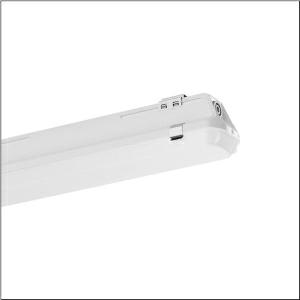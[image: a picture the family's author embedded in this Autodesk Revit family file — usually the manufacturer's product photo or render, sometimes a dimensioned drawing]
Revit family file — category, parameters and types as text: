
# Revit family: monsun_r__21_51fb10dp480b_f32f
name_source: partatom
category: Lighting Fixtures
units: mm (PartAtom-declared; Revit-internal decimal feet)

## family parameters
Cut with Voids When Loaded = No
Host = Face
Light Source = No
Part Type = Normal
Room Calculation Point = No
Round Connector Dimension = Use Diameter
Shared = No

## types (1)
- --- (1 x LED, 8090 lm, 54.4 W, 4000K)
    Apparent Load = 54 VA
    CIE Flux Codes = 47 77 93 94 100
    Color Rendering = 80
    Color Temperature = 4000K
    Default Elevation = 1800 mm
    Description = Monsun® 21, damp-proof luminaire, chain hanger, primary optical cover: enclosure, of PMMA, light emission: direct distribution, primary light characteristic: symmetric, installation type: suspended mounting, surface-mounted, horizontal mounting, vertical mounting, LED, rated luminous flux: 8.090lm, luminous efficacy: 149lm/W, light colour: 840, colour temperature: 4000K, control gear: ECG DALI, with terminal, 5-pole, max. 2.5mm², mains connection: 220..240V, AC, 50/60Hz, rated input power: 54W, housing, of glass-fibre reinforced polyester, uncoated, bright grey, incl. chain hanger, length: 1.590mm, width: 90mm, height: 88mm, clip for enclosure, of stainless steel (V2A), ceiling mounting element, of stainless steel (V2A), chain hanger, of stainless steel (V2A), protection rating (complete): IP66, insulation class (complete): insulation class I (protective earthing), certification: CE, ENEC, VDE, UKCA, protection symbol: D, impact resistance: IK04, permissible operating ambient temperature: -25..+35°C, standard: EN 50419, EN 60598-2-1, corresponds to IFS (International Featured Standards) requirements for safety and quality in the food industry, for indoor or canopied outdoor use, no direct snow, no direct sun, no direct rain, contact your sales advisor before using the luminaires in applications with unclear chemical exposure, large temperature fluctuations or condensation-forming humidity, LABS conformity tested according to VDMA 24364:2018-05, packaging unit: 1 piece
    Height = 89 mm
    Lamp = 1 x LED
    Lamp Light Flux = 8090 lm
    Lamp Power = 54.4 W
    Lamp count = 1
    Length = 1590 mm
    Luminous efficacy = 149 lm/W
    Manufacturer = Siteco
    ModVariant = No
    Model = 51FB10DP480B
    Mounting Place = Ceiling
    Mounting Type = Surface mounted
    Number of Poles = 1
    OnlyDefault = Yes
    Power Factor = 1
    Product Name = Monsun® 21
    Product group = damp-proof luminaire
    ProductGroupID = 301
    Protection Class = Protection class I
    Protection Degree = IP 66
    RLX_Detail_Level = 1
    RLX_Emergency_Light_Flux = 0 lm
    RLX_Emergency_Type = 0
    RLX_Emergency_Type_DB = No
    RlxData = <blob elided: 92413 chars, md5=a86dd47d>
    Socket = socket
    Standby Power = 0 W
    System Light Flux = 8090 lm
    System Power = 54 W
    Type Comments = factory setting: luminous flux: 100 % | dim-lin: 254 | 358 mA
    Type Image = l_1006717.jpg
    URL = http://relux.com
    VarID = @adj_152331
    Voltage = 0 V
    Weight = 0.00 kg
    Width = 90 mm

## geometry (parser evidence)
native form markers: Blend x4, Sweep x14
no freeform markers — native parametric forms only
